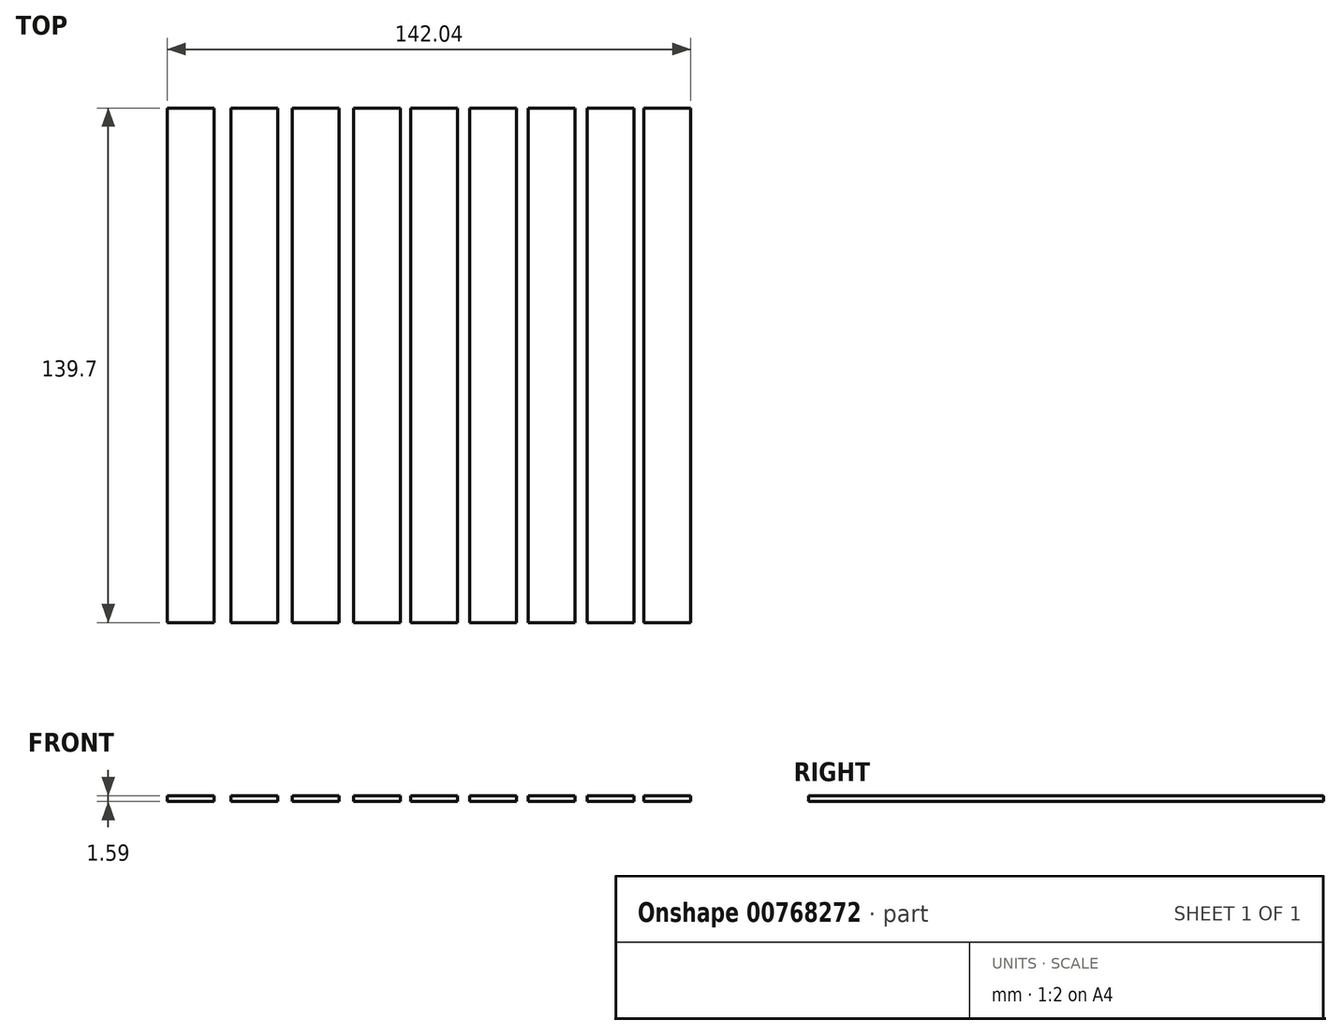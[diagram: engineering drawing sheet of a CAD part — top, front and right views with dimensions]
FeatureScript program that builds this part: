
annotation { "Feature Type Name" : "Feature", "Feature Type Description" : "" }
export const myFeature = defineFeature(function(context is Context, id is Id, definition is map)
    precondition{}
    {
        {
            var Q0;
            Q0=qCreatedBy(makeId("Top.planeOp"),FACE);
            var sketch = newSketch(context, id + "F0", { "sketchPlane" : qUnion([Q0])});
            skLineSegment(sketch, "E0.bottom", {"start": v(0, 0) * mm, "end": v(12.7, 0) * mm});
            skLineSegment(sketch, "E0.top", {"start": v(0, 139.7) * mm, "end": v(12.7, 139.7) * mm});
            skLineSegment(sketch, "E0.left", {"start": v(0, 0) * mm, "end": v(0, 139.7) * mm});
            skLineSegment(sketch, "E0.right", {"start": v(12.7, 0) * mm, "end": v(12.7, 139.7) * mm});
            skLineSegment(sketch, "E1.bottom", {"start": v(17.27, 0) * mm, "end": v(29.97, 0) * mm});
            skLineSegment(sketch, "E1.top", {"start": v(17.27, 139.7) * mm, "end": v(29.97, 139.7) * mm});
            skLineSegment(sketch, "E1.left", {"start": v(17.27, 0) * mm, "end": v(17.27, 139.7) * mm});
            skLineSegment(sketch, "E1.right", {"start": v(29.97, 0) * mm, "end": v(29.97, 139.7) * mm});
            skLineSegment(sketch, "E2.bottom", {"start": v(33.9, 0) * mm, "end": v(46.6, 0) * mm});
            skLineSegment(sketch, "E2.top", {"start": v(33.9, 139.7) * mm, "end": v(46.6, 139.7) * mm});
            skLineSegment(sketch, "E2.left", {"start": v(33.9, 0) * mm, "end": v(33.9, 139.7) * mm});
            skLineSegment(sketch, "E2.right", {"start": v(46.6, 0) * mm, "end": v(46.6, 139.7) * mm});
            skLineSegment(sketch, "E3.bottom", {"start": v(50.57, 0) * mm, "end": v(63.27, 0) * mm});
            skLineSegment(sketch, "E3.top", {"start": v(50.57, 139.7) * mm, "end": v(63.27, 139.7) * mm});
            skLineSegment(sketch, "E3.left", {"start": v(50.57, 0) * mm, "end": v(50.57, 139.7) * mm});
            skLineSegment(sketch, "E3.right", {"start": v(63.27, 0) * mm, "end": v(63.27, 139.7) * mm});
            skLineSegment(sketch, "E4.bottom", {"start": v(66.06, 0) * mm, "end": v(78.76, 0) * mm});
            skLineSegment(sketch, "E4.top", {"start": v(66.06, 139.7) * mm, "end": v(78.76, 139.7) * mm});
            skLineSegment(sketch, "E4.left", {"start": v(66.06, 0) * mm, "end": v(66.06, 139.7) * mm});
            skLineSegment(sketch, "E4.right", {"start": v(78.76, 0) * mm, "end": v(78.76, 139.7) * mm});
            skLineSegment(sketch, "E5.bottom", {"start": v(82.06, 0) * mm, "end": v(94.76, 0) * mm});
            skLineSegment(sketch, "E5.top", {"start": v(82.06, 139.7) * mm, "end": v(94.76, 139.7) * mm});
            skLineSegment(sketch, "E5.left", {"start": v(82.06, 0) * mm, "end": v(82.06, 139.7) * mm});
            skLineSegment(sketch, "E5.right", {"start": v(94.76, 0) * mm, "end": v(94.76, 139.7) * mm});
            skLineSegment(sketch, "E6.bottom", {"start": v(97.9, 0) * mm, "end": v(110.6, 0) * mm});
            skLineSegment(sketch, "E6.top", {"start": v(97.9, 139.7) * mm, "end": v(110.6, 139.7) * mm});
            skLineSegment(sketch, "E6.left", {"start": v(97.9, 0) * mm, "end": v(97.9, 139.7) * mm});
            skLineSegment(sketch, "E6.right", {"start": v(110.6, 0) * mm, "end": v(110.6, 139.7) * mm});
            skLineSegment(sketch, "E7.bottom", {"start": v(113.9, 0) * mm, "end": v(126.6, 0) * mm});
            skLineSegment(sketch, "E7.top", {"start": v(113.9, 139.7) * mm, "end": v(126.6, 139.7) * mm});
            skLineSegment(sketch, "E7.left", {"start": v(113.9, 0) * mm, "end": v(113.9, 139.7) * mm});
            skLineSegment(sketch, "E7.right", {"start": v(126.6, 0) * mm, "end": v(126.6, 139.7) * mm});
            skLineSegment(sketch, "E8.bottom", {"start": v(129.34, 0) * mm, "end": v(142.04, 0) * mm});
            skLineSegment(sketch, "E8.top", {"start": v(129.34, 139.7) * mm, "end": v(142.04, 139.7) * mm});
            skLineSegment(sketch, "E8.left", {"start": v(129.34, 0) * mm, "end": v(129.34, 139.7) * mm});
            skLineSegment(sketch, "E8.right", {"start": v(142.04, 0) * mm, "end": v(142.04, 139.7) * mm});
            skSolve(sketch);
        }
        {
            var Q0;
            Q0=makeQuery(id+"F0.imprint","IMPRINT",FACE,{"disambiguationData":[TD([[makeQuery(id+"F0.imprint","IMPRINT",EDGE,{"derivedFrom":sQuery(id+"F0.wireOp",EDGE,"E0.bottom")}),1.0]])]});
            var Q1;
            Q1=makeQuery(id+"F0.imprint","IMPRINT",FACE,{"disambiguationData":[TD([[makeQuery(id+"F0.imprint","IMPRINT",EDGE,{"derivedFrom":sQuery(id+"F0.wireOp",EDGE,"E1.bottom")}),1.0]])]});
            var Q2;
            Q2=makeQuery(id+"F0.imprint","IMPRINT",FACE,{"disambiguationData":[TD([[makeQuery(id+"F0.imprint","IMPRINT",EDGE,{"derivedFrom":sQuery(id+"F0.wireOp",EDGE,"E2.bottom")}),1.0]])]});
            var Q3;
            Q3=makeQuery(id+"F0.imprint","IMPRINT",FACE,{"disambiguationData":[TD([[makeQuery(id+"F0.imprint","IMPRINT",EDGE,{"derivedFrom":sQuery(id+"F0.wireOp",EDGE,"E3.bottom")}),1.0]])]});
            var Q4;
            Q4=makeQuery(id+"F0.imprint","IMPRINT",FACE,{"disambiguationData":[TD([[makeQuery(id+"F0.imprint","IMPRINT",EDGE,{"derivedFrom":sQuery(id+"F0.wireOp",EDGE,"E4.bottom")}),1.0]])]});
            var Q5;
            Q5=makeQuery(id+"F0.imprint","IMPRINT",FACE,{"disambiguationData":[TD([[makeQuery(id+"F0.imprint","IMPRINT",EDGE,{"derivedFrom":sQuery(id+"F0.wireOp",EDGE,"E5.bottom")}),1.0]])]});
            var Q6;
            Q6=makeQuery(id+"F0.imprint","IMPRINT",FACE,{"disambiguationData":[TD([[makeQuery(id+"F0.imprint","IMPRINT",EDGE,{"derivedFrom":sQuery(id+"F0.wireOp",EDGE,"E6.bottom")}),1.0]])]});
            var Q7;
            Q7=makeQuery(id+"F0.imprint","IMPRINT",FACE,{"disambiguationData":[TD([[makeQuery(id+"F0.imprint","IMPRINT",EDGE,{"derivedFrom":sQuery(id+"F0.wireOp",EDGE,"E7.bottom")}),1.0]])]});
            var Q8;
            Q8=makeQuery(id+"F0.imprint","IMPRINT",FACE,{"disambiguationData":[TD([[makeQuery(id+"F0.imprint","IMPRINT",EDGE,{"derivedFrom":sQuery(id+"F0.wireOp",EDGE,"E8.bottom")}),1.0]])]});
            extrude(context, id + "F1", {"entities" : qUnion([Q0, Q1, Q2, Q3, Q4, Q5, Q6, Q7, Q8]), "depth" : 1.59 * mm, "offsetDistance" : 25.4 * mm});
        }
    });
